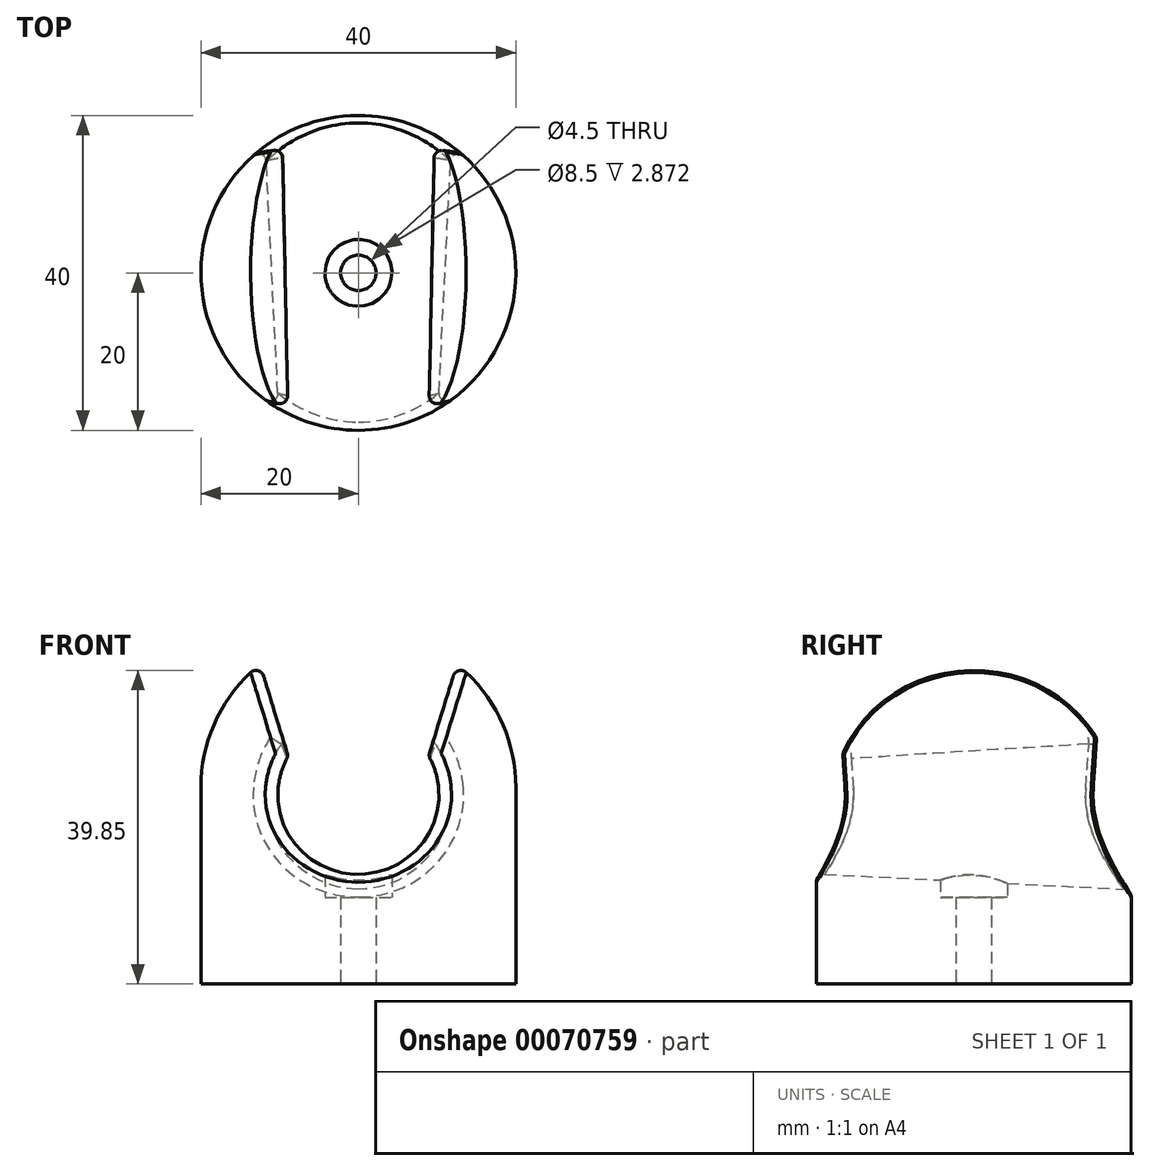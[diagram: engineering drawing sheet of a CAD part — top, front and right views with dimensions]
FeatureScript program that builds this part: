
annotation { "Feature Type Name" : "Feature", "Feature Type Description" : "" }
export const myFeature = defineFeature(function(context is Context, id is Id, definition is map)
    precondition{}
    {
        {
            var Q0;
            Q0=qCreatedBy(makeId("Front.planeOp"),FACE);
            var sketch = newSketch(context, id + "F0", { "sketchPlane" : qUnion([Q0])});
            skLineSegment(sketch, "E0.bottom", {"start": v(0, 45) * mm, "end": v(0, 45) * mm});
            skLineSegment(sketch, "E0.top", {"start": v(-20, 0) * mm, "end": v(20, 0) * mm});
            skLineSegment(sketch, "E0.left", {"start": v(-20, 25) * mm, "end": v(-20, 0) * mm});
            skLineSegment(sketch, "E0.right", {"start": v(20, 25) * mm, "end": v(20, 0) * mm});
            skPoint(sketch, "E1.visualSharp", {"position": v(20, 45) * mm});
            skArc(sketch, "E1.filletArc", {"start": v(20, 25) * mm, "mid": v(14.14, 39.14) * mm, "end": v(0, 45) * mm});
            skPoint(sketch, "E2.visualSharp", {"position": v(-20, 45) * mm});
            skArc(sketch, "E2.filletArc", {"start": v(0, 45) * mm, "mid": v(-14.14, 39.14) * mm, "end": v(-20, 25) * mm});
            skLineSegment(sketch, "E3", {"start": v(-12.5, 0) * mm, "end": v(-12.5, 40.61) * mm});
            skLineSegment(sketch, "E4", {"start": v(0, 0) * mm, "end": v(-12.5, 40.61) * mm});
            skLineSegment(sketch, "E5", {"start": v(12.5, 0) * mm, "end": v(12.5, 40.61) * mm});
            skLineSegment(sketch, "E6", {"start": v(0, 0) * mm, "end": v(12.5, 40.61) * mm});
            skLineSegment(sketch, "E7", {"start": v(-20, 25) * mm, "end": v(20, 25) * mm});
            skSolve(sketch);
        }
        {
            var Q0;
            {var subQ0=sQuery(id+"F0.wireOp",EDGE,"E0.left");Q0=makeQuery(id+"F0.imprint","IMPRINT",FACE,{"disambiguationData":[TD([[makeQuery(id+"F0.imprint","IMPRINT",EDGE,{"derivedFrom":subQ0}),1.0]])]});}
            var Q1;
            {var subQ0=sQuery(id+"F0.wireOp",EDGE,"E3");Q1=makeQuery(id+"F0.imprint","IMPRINT",FACE,{"disambiguationData":[TD([[makeQuery(id+"F0.imprint","IMPRINT",EDGE,{"derivedFrom":subQ0}),-1.0]])]});}
            var Q2;
            {var subQ2=sQuery(id+"F0.wireOp",EDGE,"E5");Q2=makeQuery(id+"F0.imprint","IMPRINT",FACE,{"disambiguationData":[TD([[makeQuery(id+"F0.imprint","IMPRINT",EDGE,{"derivedFrom":subQ2}),1.0]])]});}
            var Q3;
            {var subQ0=sQuery(id+"F0.wireOp",EDGE,"E0.right");Q3=makeQuery(id+"F0.imprint","IMPRINT",FACE,{"disambiguationData":[TD([[makeQuery(id+"F0.imprint","IMPRINT",EDGE,{"derivedFrom":subQ0}),-1.0]])]});}
            var Q4;
            {var subQ4=sQuery(id+"F0.wireOp",EDGE,"E4");Q4=makeQuery(id+"F0.imprint","IMPRINT",FACE,{"disambiguationData":[TD([[makeQuery(id+"F0.imprint","IMPRINT",EDGE,{"derivedFrom":subQ4}),-1.0]])]});}
            var Q5;
            {var subQ0=sQuery(id+"F0.wireOp",EDGE,"E7");var subQ3=sQuery(id+"F0.wireOp",EDGE,"E3");var subQ5=makeQuery(id+"F0.imprint","INTERSECT",VERTEX,{"derivedFrom":[subQ3,subQ0]});Q5=makeQuery(id+"F0.imprint","IMPRINT",FACE,{"disambiguationData":[TD([[makeQuery(id+"F0.imprint","IMPRINT",EDGE,{"disambiguationData":[TD([[subQ5,-1.0]])],"derivedFrom":subQ3}),1.0]])]});}
            var Q6;
            {var subQ0=sQuery(id+"F0.wireOp",EDGE,"E7");var subQ3=sQuery(id+"F0.wireOp",EDGE,"E5");var subQ5=makeQuery(id+"F0.imprint","INTERSECT",VERTEX,{"derivedFrom":[subQ3,subQ0]});Q6=makeQuery(id+"F0.imprint","IMPRINT",FACE,{"disambiguationData":[TD([[makeQuery(id+"F0.imprint","IMPRINT",EDGE,{"disambiguationData":[TD([[subQ5,-1.0]])],"derivedFrom":subQ3}),-1.0]])]});}
            var Q7;
            {var subQ1=sQuery(id+"F0.wireOp",EDGE,"E0.top");var subQ3=sQuery(id+"F0.wireOp",EDGE,"E5");var subQ4=makeQuery(id+"F0.imprint","INTERSECT",VERTEX,{"derivedFrom":[subQ1,subQ3]});Q7=makeQuery(id+"F0.imprint","IMPRINT",FACE,{"disambiguationData":[TD([[makeQuery(id+"F0.imprint","IMPRINT",EDGE,{"disambiguationData":[TD([[subQ4,-1.0]])],"derivedFrom":subQ3}),1.0]])]});}
            var Q8;
            {var subQ0=sQuery(id+"F0.wireOp",EDGE,"E3");var subQ1=sQuery(id+"F0.wireOp",EDGE,"E0.top");var subQ2=makeQuery(id+"F0.imprint","INTERSECT",VERTEX,{"derivedFrom":[subQ1,subQ0]});Q8=makeQuery(id+"F0.imprint","IMPRINT",FACE,{"disambiguationData":[TD([[makeQuery(id+"F0.imprint","IMPRINT",EDGE,{"disambiguationData":[TD([[subQ2,-1.0]])],"derivedFrom":subQ0}),-1.0]])]});}
            extrude(context, id + "F1", {"entities" : qUnion([Q0, Q1, Q2, Q3, Q4, Q5, Q6, Q7, Q8]), "endBound" : BoundingType.SYMMETRIC, "depth" : 40 * mm, "hasSecondDirection" : true, "secondDirectionOppositeDirection" : true, "secondDirectionDepth" : 25 * mm});
        }
        {
            var Q0;
            Q0=makeQuery(id+"F1.opExtrude","CAP_FACE",FACE,{"disambiguationData":[OSD([sQuery(id+"F0.wireOp",EDGE,"E0.top"),sQuery(id+"F0.wireOp",EDGE,"E0.left"),sQuery(id+"F0.wireOp",EDGE,"E0.right"),sQuery(id+"F0.wireOp",EDGE,"E1.filletArc"),sQuery(id+"F0.wireOp",EDGE,"E2.filletArc")])],"isStart":false});
            var sketch = newSketch(context, id + "F2", { "sketchPlane" : qUnion([Q0])});
            skCircle(sketch, "E8", {"center": v(0, 24) * mm, "radius": 10 * mm});
            skSolve(sketch);
        }
        {
            var Q0;
            Q0=makeQuery(id+"F2.imprint","IMPRINT",FACE,{"disambiguationData":[TD([[makeQuery(id+"F2.imprint","IMPRINT",EDGE,{"derivedFrom":sQuery(id+"F2.wireOp",EDGE,"E8")}),1.0]])]});
            extrude(context, id + "F3", {"entities" : qUnion([Q0]), "operationType" : NewBodyOperationType.REMOVE, "oppositeDirection" : true, "depth" : 40 * mm, "hasDraft" : true, "draftAngle" : 2.86 * degree});
        }
        {
            var Q0;
            Q0=makeQuery(id+"F1.opExtrude","CAP_EDGE",EDGE,{"disambiguationData":[OSD([sQuery(id+"F0.wireOp",EDGE,"E0.left")])],"isStart":false});
            var Q1;
            Q1=makeQuery(id+"F1.opExtrude","CAP_EDGE",EDGE,{"disambiguationData":[OSD([sQuery(id+"F0.wireOp",EDGE,"E0.right")])],"isStart":false});
            var Q2;
            Q2=makeQuery(id+"F1.opExtrude","CAP_EDGE",EDGE,{"disambiguationData":[OSD([sQuery(id+"F0.wireOp",EDGE,"E1.filletArc")])],"isStart":false});
            var Q3;
            Q3=makeQuery(id+"F1.opExtrude","CAP_EDGE",EDGE,{"disambiguationData":[OSD([sQuery(id+"F0.wireOp",EDGE,"E2.filletArc")])],"isStart":false});
            var Q4;
            Q4=makeQuery(id+"F1.opExtrude","CAP_EDGE",EDGE,{"disambiguationData":[OSD([sQuery(id+"F0.wireOp",EDGE,"E0.left")])],"isStart":true});
            var Q5;
            Q5=makeQuery(id+"F1.opExtrude","CAP_EDGE",EDGE,{"disambiguationData":[OSD([sQuery(id+"F0.wireOp",EDGE,"E2.filletArc")])],"isStart":true});
            var Q6;
            Q6=makeQuery(id+"F1.opExtrude","CAP_EDGE",EDGE,{"disambiguationData":[OSD([sQuery(id+"F0.wireOp",EDGE,"E1.filletArc")])],"isStart":true});
            var Q7;
            Q7=makeQuery(id+"F1.opExtrude","CAP_EDGE",EDGE,{"disambiguationData":[OSD([sQuery(id+"F0.wireOp",EDGE,"E0.right")])],"isStart":true});
            fillet(context, id + "F4", {"entities" : qUnion([Q0, Q1, Q2, Q3, Q4, Q5, Q6, Q7]), "radius" : 20 * mm, "tangentPropagation" : true, "allowEdgeOverflow" : false});
        }
        {
            var Q0;
            Q0=makeQuery(id+"F1.opExtrude","SWEPT_FACE",FACE,{"disambiguationData":[OSD([sQuery(id+"F0.wireOp",EDGE,"E4")])]});
            var Q1;
            Q1=makeQuery(id+"F1.opExtrude","SWEPT_FACE",FACE,{"disambiguationData":[OSD([sQuery(id+"F0.wireOp",EDGE,"E6")])]});
            var Q2;
            Q2=makeQuery(id+"F3.boolean.opBoolean","COPY",FACE,{"derivedFrom":makeQuery(id+"F3.opExtrude","SWEPT_FACE",FACE,{"disambiguationData":[OSD([sQuery(id+"F2.wireOp",EDGE,"E8")])]})});
            fillet(context, id + "F5", {"entities" : qUnion([Q0, Q1, Q2]), "radius" : 1 * mm, "tangentPropagation" : true, "allowEdgeOverflow" : false});
        }
        {
            var Q0;
            Q0=makeQuery(id+"F1.opExtrude","SWEPT_FACE",FACE,{"disambiguationData":[OSD([sQuery(id+"F0.wireOp",EDGE,"E0.top")])]});
            var sketch = newSketch(context, id + "F6", { "sketchPlane" : qUnion([Q0])});
            skCircle(sketch, "E9", {"center": v(0, 0) * mm, "radius": 2.25 * mm});
            skCircle(sketch, "E10", {"center": v(0, 0) * mm, "radius": 4.25 * mm});
            skSolve(sketch);
        }
        {
            var Q0;
            Q0=makeQuery(id+"F6.imprint","IMPRINT",FACE,{"disambiguationData":[TD([[makeQuery(id+"F6.imprint","IMPRINT",EDGE,{"derivedFrom":sQuery(id+"F6.wireOp",EDGE,"E9")}),1.0]])]});
            extrude(context, id + "F7", {"entities" : qUnion([Q0]), "operationType" : NewBodyOperationType.REMOVE, "endBound" : BoundingType.THROUGH_ALL, "oppositeDirection" : true, "depth" : 25 * mm});
        }
        {
            var Q0;
            Q0=makeQuery(id+"F6.imprint","IMPRINT",FACE,{"disambiguationData":[TD([[makeQuery(id+"F6.imprint","IMPRINT",EDGE,{"derivedFrom":sQuery(id+"F6.wireOp",EDGE,"E9")}),-1.0]])]});
            extrude(context, id + "F8", {"entities" : qUnion([Q0]), "operationType" : NewBodyOperationType.REMOVE, "endBound" : BoundingType.UP_TO_NEXT, "oppositeDirection" : true, "depth" : 14 * mm, "hasSecondDirection" : true, "secondDirectionOppositeDirection" : true, "secondDirectionDepth" : 11 * mm});
        }
    });
